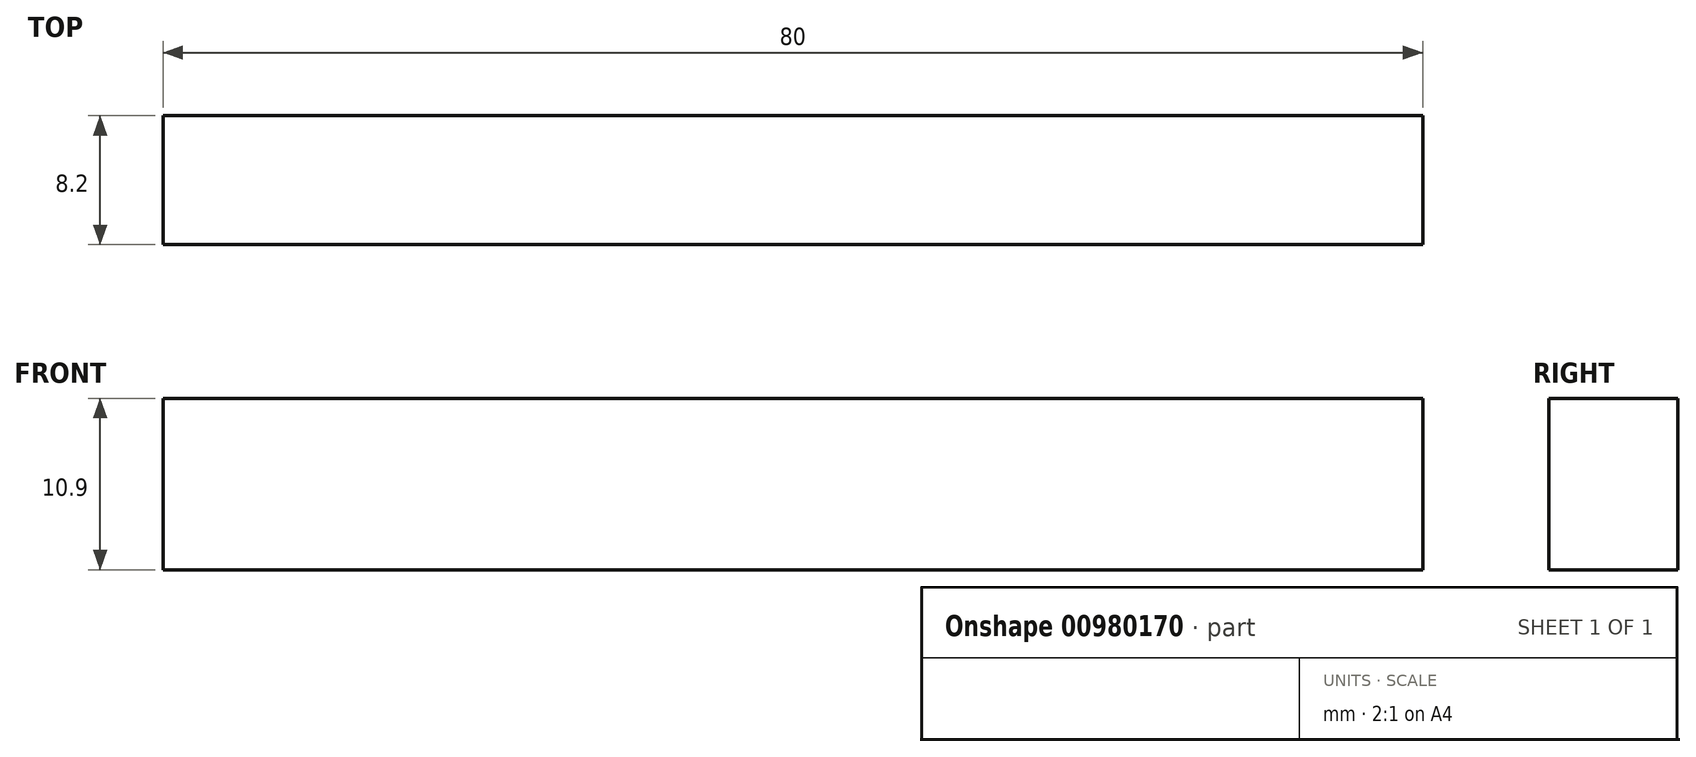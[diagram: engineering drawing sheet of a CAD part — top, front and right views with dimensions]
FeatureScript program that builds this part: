
annotation { "Feature Type Name" : "Feature", "Feature Type Description" : "" }
export const myFeature = defineFeature(function(context is Context, id is Id, definition is map)
    precondition{}
    {
        {
            var Q0;
            Q0=qCreatedBy(makeId("Top.planeOp"),FACE);
            var sketch = newSketch(context, id + "F0", { "sketchPlane" : qUnion([Q0])});
            skLineSegment(sketch, "E0.bottom", {"start": v(-40, 4.1) * mm, "end": v(40, 4.1) * mm});
            skLineSegment(sketch, "E0.top", {"start": v(-40, -4.1) * mm, "end": v(40, -4.1) * mm});
            skLineSegment(sketch, "E0.left", {"start": v(-40, 4.1) * mm, "end": v(-40, -4.1) * mm});
            skLineSegment(sketch, "E0.right", {"start": v(40, 4.1) * mm, "end": v(40, -4.1) * mm});
            skPoint(sketch, "E0.middle", {"position": v(0, 0) * mm});
            skSolve(sketch);
        }
        {
            var Q0;
            Q0 = qSketchRegion(id + "F0", true);
            extrude(context, id + "F1", {"entities" : qUnion([Q0]), "depth" : 10.9 * mm, "offsetDistance" : 25 * mm});
        }
    });
